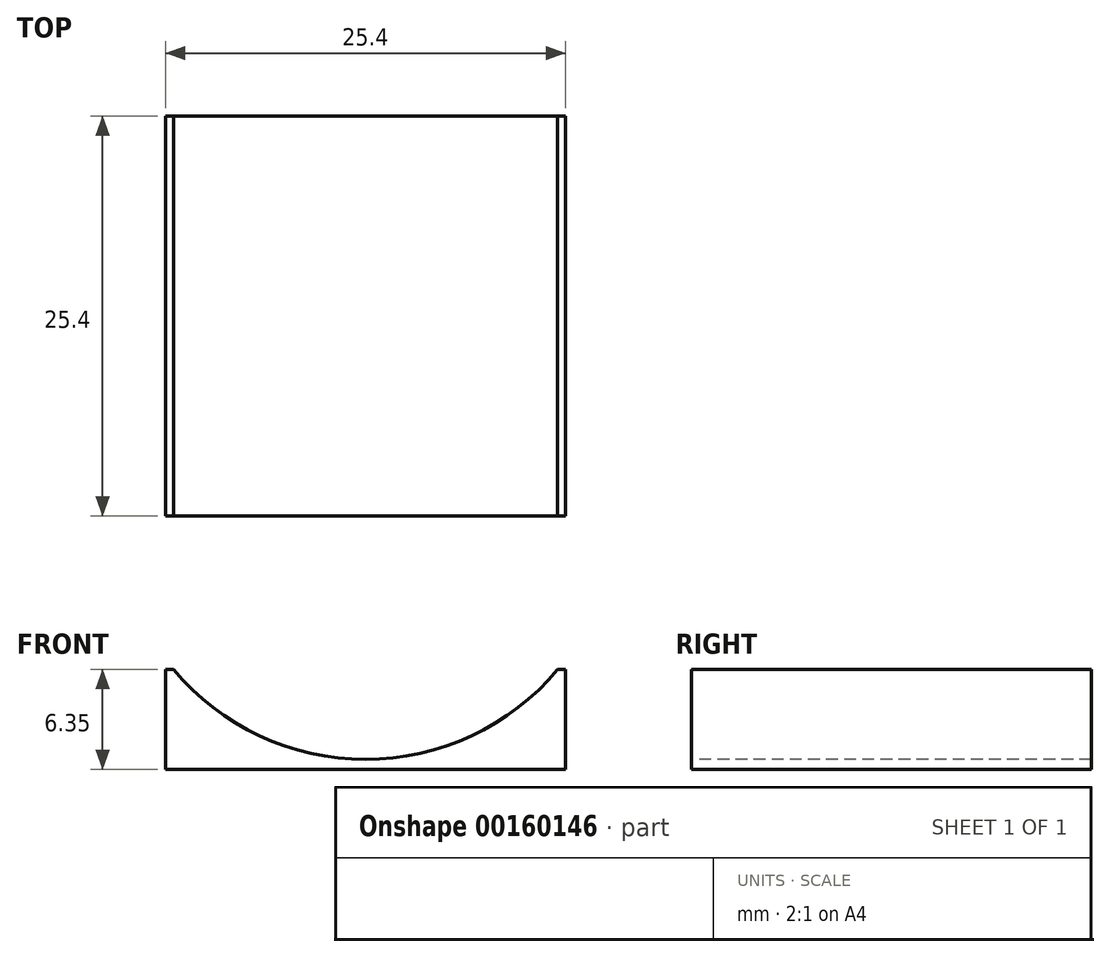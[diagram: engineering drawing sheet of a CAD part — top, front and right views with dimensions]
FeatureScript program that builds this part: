
annotation { "Feature Type Name" : "Feature", "Feature Type Description" : "" }
export const myFeature = defineFeature(function(context is Context, id is Id, definition is map)
    precondition{}
    {
        {
            var Q0;
            Q0=qCreatedBy(makeId("Top.planeOp"),FACE);
            var sketch = newSketch(context, id + "F0", { "sketchPlane" : qUnion([Q0])});
            skLineSegment(sketch, "E0.bottom", {"start": v(12.7, -12.7) * mm, "end": v(-12.7, -12.7) * mm});
            skLineSegment(sketch, "E0.top", {"start": v(12.7, 12.7) * mm, "end": v(-12.7, 12.7) * mm});
            skLineSegment(sketch, "E0.left", {"start": v(12.7, -12.7) * mm, "end": v(12.7, 12.7) * mm});
            skLineSegment(sketch, "E0.right", {"start": v(-12.7, -12.7) * mm, "end": v(-12.7, 12.7) * mm});
            skPoint(sketch, "E0.middle", {"position": v(0, 0) * mm});
            skSolve(sketch);
        }
        {
            var Q0;
            Q0 = qSketchRegion(id + "F0", true);
            extrude(context, id + "F1", {"entities" : qUnion([Q0]), "depth" : 6.35 * mm});
        }
        {
            var Q0;
            Q0=makeQuery(id+"F1.opExtrude","SWEPT_FACE",FACE,{"disambiguationData":[OSD([sQuery(id+"F0.wireOp",EDGE,"E0.bottom")])]});
            var sketch = newSketch(context, id + "F2", { "sketchPlane" : qUnion([Q0])});
            skLineSegment(sketch, "E1", {"start": v(0, 0) * mm, "end": v(0, 26.3) * mm, "construction": true});
            skPoint(sketch, "E1.endSnap0", {"position": v(0, 6.35) * mm});
            skLineSegment(sketch, "E2", {"start": v(-19.88, 16.51) * mm, "end": v(26.54, 16.51) * mm, "construction": true});
            skCircle(sketch, "E3", {"center": v(0, 16.51) * mm, "radius": 15.88 * mm});
            skSolve(sketch);
        }
        {
            var Q0;
            Q0 = qSketchRegion(id + "F2", true);
            extrude(context, id + "F3", {"entities" : qUnion([Q0]), "operationType" : NewBodyOperationType.REMOVE, "endBound" : BoundingType.THROUGH_ALL, "oppositeDirection" : true, "depth" : 25.4 * mm});
        }
    });
